# Revit family: KS ALU-PU 80, DS 30, m.Blz, M10-M12, Ø 17,2-168,3
name_source: partatom
category: HLS-Bauteile
units: mm (PartAtom-declared; Revit-internal decimal feet)

## family parameters
Arbeitsebenenbasiert = Ja
Beim Laden mit Abzugskörper schneiden = Nein
Bemaßung runder Anschluss = Durchmesser verwenden
Beschriftungsausrichtung beibehalten = Nein
Gemeinsam genutzt = Ja
Immer vertikal = Nein
Raumberechnungspunkt = Nein
Teiletyp = Normal

## types (19) — shared parameters
Anschluss = M10/M12
Baustoffklasse = B2
DS = 30 mm  [stored 0.0984252 ft]
DVS = 18 mm  [stored 0.0590551 ft]
Dichte Kern = 80 kg/m³
Dichte Mantel = 2700 kg/m³
Dicke Mantel = 0.08 mm
Druckverteilung = Blechzylinder
Dämmkörper = ALU/PU
Dämmstärke = 30 mm  [stored 0.0984252 ft]
Fabrikat = MEFA
Firma = MEFA Befestigungs- und Montagesysteme GmbH
HGA = 22 mm  [stored 0.0721785 ft]
Kurztext1 = Kälteschelle RG80 ALU/PU
L = 100 mm
Material = Stahl
Material Mantel = Alufolie
Materialname = S235
Mengeneinheit = St
Oberflaeche = galvanisch verzinkt
Rohrschellentyp = Maxima PSM
Schalenlänge = 100 mm
Vorgabe-Ansicht = 1219 mm
Wasserdampfdiffusionswiderstand = 18750 µ
Wärmeleitfähigkeit = 0.025 W/mK
max. Temperaturbeständigkeit = 120 °C
mittl. Nenndruckfestigkeit Kern = 0.5 N/mm²
stat. Belastung Kern = 0.1 N/mm²
vpe = 1

## per-type parameters (varying)
- Kälteschelle ALU-PU 80, DS 30, m.Blz, M10/M12, Ø 17,2: A=55 mm  [stored 0.180446 ft]; AB=2 mm  [stored 0.00656168 ft]; Anschlußhöhe=55 mm; Artikelnummer=7590182/B; B=135 mm; Breite=141 mm; D=18 mm  [stored 0.0590551 ft]; D0=78 mm; DF1=25 mm  [stored 0.082021 ft]; DF2=25 mm  [stored 0.082021 ft]; Dmax=19 mm  [stored 0.062336 ft]; Dmin=16 mm  [stored 0.0524934 ft]; EAN=4250928443878; Gewicht=0.54 kg; Gewicht pro Bauteil=0.54 kg; H=106 mm; Kurztext2=17,2 mm Iso 30 x 100 mm M10/M12; MB=30 mm  [stored 0.0984252 ft]; MD=3 mm  [stored 0.00984252 ft]; R=39 mm  [stored 0.127953 ft]; RM=42 mm  [stored 0.137795 ft]; Rohraußendurchmesser Kupfer=18 mm; Rohraußendurchmesser Stahl=17,2 mm; S=110 mm; max. zul. Last=0.30 kN
- Kälteschelle ALU-PU 80, DS 30, m.Blz, M10/M12, Ø 21,3: A=55 mm  [stored 0.180446 ft]; AB=2 mm  [stored 0.00656168 ft]; Anschlußhöhe=56 mm; Artikelnummer=75902142/B; B=150 mm; Breite=151 mm; D=22 mm  [stored 0.0721785 ft]; D0=82 mm; DF1=30 mm  [stored 0.0984252 ft]; DF2=29 mm  [stored 0.0951444 ft]; Dmax=25 mm  [stored 0.082021 ft]; Dmin=20 mm  [stored 0.0656168 ft]; EAN=4250928443892; Gewicht=0.57 kg; Gewicht pro Bauteil=0.57 kg; H=110 mm; Kurztext2=21,3 mm Iso 30 x 100 mm M10/M12; MB=30 mm  [stored 0.0984252 ft]; MD=3 mm  [stored 0.00984252 ft]; R=41 mm  [stored 0.134514 ft]; RM=44 mm  [stored 0.144357 ft]; Rohraußendurchmesser Kupfer=22 mm; Rohraußendurchmesser Stahl=21,3 mm; S=120 mm; max. zul. Last=0.30 kN
- Kälteschelle ALU-PU 80, DS 30, m.Blz, M10/M12, Ø 26,9: A=55 mm  [stored 0.180446 ft]; AB=3 mm  [stored 0.00984252 ft]; Anschlußhöhe=55 mm; Artikelnummer=75902742/B; B=150 mm; Breite=151 mm; D=28 mm  [stored 0.0918635 ft]; D0=88 mm; DF1=27 mm  [stored 0.0885827 ft]; DF2=27 mm  [stored 0.0885827 ft]; Dmax=30 mm  [stored 0.0984252 ft]; Dmin=25 mm  [stored 0.082021 ft]; EAN=4250928443915; Gewicht=0.58 kg; Gewicht pro Bauteil=0.58 kg; H=116 mm; Kurztext2=26,9 mm Iso 30 x 100 mm M10/M12; MB=30 mm  [stored 0.0984252 ft]; MD=3 mm  [stored 0.00984252 ft]; R=44 mm  [stored 0.144357 ft]; RM=47 mm  [stored 0.154199 ft]; Rohraußendurchmesser Kupfer=28 mm; Rohraußendurchmesser Stahl=26,9 mm; S=123 mm; max. zul. Last=0.40 kN
- Kälteschelle ALU-PU 80, DS 30, m.Blz, M10/M12, Ø 33,7: A=55 mm  [stored 0.180446 ft]; AB=3 mm  [stored 0.00984252 ft]; Anschlußhöhe=56 mm; Artikelnummer=75903442/B; B=162 mm; Breite=162 mm; D=35 mm  [stored 0.114829 ft]; D0=95 mm; DF1=30 mm  [stored 0.0984252 ft]; DF2=30 mm  [stored 0.0984252 ft]; Dmax=36 mm  [stored 0.11811 ft]; Dmin=32 mm  [stored 0.104987 ft]; EAN=4250928443939; Gewicht=0.62 kg; Gewicht pro Bauteil=0.62 kg; H=123 mm; Kurztext2=33,7 mm Iso 30 x 100 mm M10/M12; MB=30 mm  [stored 0.0984252 ft]; MD=3 mm  [stored 0.00984252 ft]; R=48 mm; RM=51 mm; Rohraußendurchmesser Kupfer=35 mm; Rohraußendurchmesser Stahl=33,7 mm; S=132 mm; max. zul. Last=0.50 kN
- Kälteschelle ALU-PU 80, DS 30, m.Blz, M10/M12, Ø 42,4: A=55 mm  [stored 0.180446 ft]; AB=2 mm  [stored 0.00656168 ft]; Anschlußhöhe=57 mm; Artikelnummer=75904242/B; B=172 mm; Breite=172 mm; D=42 mm  [stored 0.137795 ft]; D0=102 mm; DF1=31 mm  [stored 0.101706 ft]; DF2=31 mm  [stored 0.101706 ft]; Dmax=44 mm  [stored 0.144357 ft]; Dmin=40 mm  [stored 0.131234 ft]; EAN=4250928443953; Gewicht=0.67 kg; Gewicht pro Bauteil=0.67 kg; H=130 mm; Kurztext2=42,4 mm Iso 30 x 100 mm M10/M12; MB=30 mm  [stored 0.0984252 ft]; MD=3 mm  [stored 0.00984252 ft]; R=51 mm; RM=54 mm  [stored 0.177165 ft]; Rohraußendurchmesser Kupfer=42 mm; Rohraußendurchmesser Stahl=42,4 mm; S=141 mm; max. zul. Last=0.60 kN
- Kälteschelle ALU-PU 80, DS 30, m.Blz, M10/M12, Ø 48,3: A=55 mm  [stored 0.180446 ft]; AB=2 mm  [stored 0.00656168 ft]; Anschlußhöhe=55 mm; Artikelnummer=75904842/B; B=172 mm; Breite=172 mm; D=48 mm; D0=108 mm; DF1=28 mm  [stored 0.0918635 ft]; DF2=28 mm  [stored 0.0918635 ft]; Dmax=50 mm  [stored 0.164042 ft]; Dmin=46 mm  [stored 0.150919 ft]; EAN=4250928443977; Gewicht=0.67 kg; Gewicht pro Bauteil=0.67 kg; H=136 mm; Kurztext2=48,3 mm Iso 30 x 100 mm M10/M12; MB=30 mm  [stored 0.0984252 ft]; MD=3 mm  [stored 0.00984252 ft]; R=54 mm  [stored 0.177165 ft]; RM=57 mm  [stored 0.187008 ft]; Rohraußendurchmesser Stahl=48,3 mm; S=144 mm; max. zul. Last=0.70 kN
- Kälteschelle ALU-PU 80, DS 30, m.Blz, M10/M12, Ø 54: A=55 mm  [stored 0.180446 ft]; AB=4 mm  [stored 0.0131234 ft]; Anschlußhöhe=55 mm; Artikelnummer=75905442/B; B=178 mm; Breite=178 mm; D=54 mm  [stored 0.177165 ft]; D0=114 mm; DF1=28 mm  [stored 0.0918635 ft]; DF2=28 mm  [stored 0.0918635 ft]; Dmax=56 mm  [stored 0.183727 ft]; Dmin=50 mm  [stored 0.164042 ft]; EAN=4250928443991; Gewicht=0.71 kg; Gewicht pro Bauteil=0.71 kg; H=142 mm; Kurztext2=54 mm Iso 30 x 100 mm M10/M12; MB=30 mm  [stored 0.0984252 ft]; MD=3 mm  [stored 0.00984252 ft]; R=57 mm  [stored 0.187008 ft]; RM=60 mm; Rohraußendurchmesser Kupfer=54 mm; S=150 mm; max. zul. Last=0.70 kN
- Kälteschelle ALU-PU 80, DS 30, m.Blz, M10/M12, Ø 57: A=55 mm  [stored 0.180446 ft]; AB=2 mm  [stored 0.00656168 ft]; Anschlußhöhe=54 mm; Artikelnummer=75905742/B; B=178 mm; Breite=178 mm; D=57 mm  [stored 0.187008 ft]; D0=117 mm; DF1=28 mm  [stored 0.0918635 ft]; DF2=27 mm  [stored 0.0885827 ft]; Dmax=57 mm  [stored 0.187008 ft]; Dmin=55 mm  [stored 0.180446 ft]; EAN=4250928444011; Gewicht=0.71 kg; Gewicht pro Bauteil=0.71 kg; H=145 mm; Kurztext2=57 mm Iso 30 x 100 mm M10/M12; MB=30 mm  [stored 0.0984252 ft]; MD=3 mm  [stored 0.00984252 ft]; R=59 mm; RM=62 mm  [stored 0.203412 ft]; Rohraußendurchmesser Stahl=57 mm; S=150 mm; max. zul. Last=0.80 kN
- Kälteschelle ALU-PU 80, DS 30, m.Blz, M10/M12, Ø 60,3: A=55 mm  [stored 0.180446 ft]; AB=2 mm  [stored 0.00656168 ft]; Anschlußhöhe=55 mm; Artikelnummer=75906042/B; B=184 mm; Breite=184 mm; D=60 mm; D0=120 mm; DF1=28 mm  [stored 0.0918635 ft]; DF2=28 mm  [stored 0.0918635 ft]; Dmax=62 mm  [stored 0.203412 ft]; Dmin=58 mm  [stored 0.190289 ft]; EAN=4250928444035; Gewicht=0.73 kg; Gewicht pro Bauteil=0.73 kg; H=148 mm; Kurztext2=60,3 mm Iso 30 x 100 mm M10/M12; MB=30 mm  [stored 0.0984252 ft]; MD=3 mm  [stored 0.00984252 ft]; R=60 mm; RM=63 mm; Rohraußendurchmesser Stahl=60,3 mm; S=156 mm; max. zul. Last=0.90 kN
- Kälteschelle ALU-PU 80, DS 30, m.Blz, M10/M12, Ø 63,5: A=55 mm  [stored 0.180446 ft]; AB=3 mm  [stored 0.00984252 ft]; Anschlußhöhe=56 mm; Artikelnummer=75906442/B; B=189 mm; Breite=189 mm; D=64 mm  [stored 0.209974 ft]; D0=124 mm; DF1=30 mm  [stored 0.0984252 ft]; DF2=29 mm  [stored 0.0951444 ft]; Dmax=64 mm  [stored 0.209974 ft]; Dmin=61 mm  [stored 0.200131 ft]; EAN=4250928444059; Gewicht=0.76 kg; Gewicht pro Bauteil=0.76 kg; H=152 mm; Kurztext2=63,5 mm Iso 30 x 100 mm M10/M12; MB=30 mm  [stored 0.0984252 ft]; MD=3 mm  [stored 0.00984252 ft]; R=62 mm  [stored 0.203412 ft]; RM=65 mm; Rohraußendurchmesser Stahl=63,5 mm; S=159 mm; max. zul. Last=0.90 kN
- Kälteschelle ALU-PU 80, DS 30, m.Blz, M10/M12, Ø 76,1: A=56 mm  [stored 0.183727 ft]; AB=2 mm  [stored 0.00656168 ft]; Anschlußhöhe=57 mm; Artikelnummer=75907644/B; B=217 mm; Breite=216 mm; D=76 mm; D0=136 mm; DF1=35 mm  [stored 0.114829 ft]; DF2=36 mm  [stored 0.11811 ft]; Dmax=78 mm; Dmin=74 mm; EAN=4250928444097; Gewicht=1.03 kg; Gewicht pro Bauteil=1.03 kg; H=166 mm; Kurztext2=76,1 mm Iso 30 x 100 mm M10/M12; MB=35 mm  [stored 0.114829 ft]; MD=4 mm  [stored 0.0131234 ft]; R=68 mm; RM=72 mm; Rohraußendurchmesser Stahl=76,1 mm; S=182 mm; max. zul. Last=1.10 kN
- Kälteschelle ALU-PU 80, DS 30, m.Blz, M10/M12, Ø 88,9: A=56 mm  [stored 0.183727 ft]; AB=1 mm  [stored 0.00328084 ft]; Anschlußhöhe=56 mm; Artikelnummer=75908944/B; B=227 mm; Breite=226 mm; D=89 mm; D0=149 mm; DF1=34 mm; DF2=35 mm  [stored 0.114829 ft]; Dmax=90 mm; Dmin=88 mm; EAN=4250928444110; Gewicht=1.12 kg; Gewicht pro Bauteil=1.12 kg; H=179 mm; Kurztext2=88,9 mm Iso 30 x 100 mm M10/M12; MB=35 mm  [stored 0.114829 ft]; MD=4 mm  [stored 0.0131234 ft]; R=74 mm; RM=78 mm; Rohraußendurchmesser Stahl=88,9 mm; S=193 mm; max. zul. Last=1.30 kN
- Kälteschelle ALU-PU 80, DS 30, m.Blz, M10/M12, Ø108: A=56 mm  [stored 0.183727 ft]; AB=2 mm  [stored 0.00656168 ft]; Anschlußhöhe=57 mm; Artikelnummer=75910844/B; B=248 mm; Breite=247 mm; D=108 mm; D0=168 mm; DF1=35 mm  [stored 0.114829 ft]; DF2=35 mm  [stored 0.114829 ft]; Dmax=110 mm; Dmin=106 mm; EAN=4250928444134; Gewicht=1.22 kg; Gewicht pro Bauteil=1.22 kg; H=198 mm; Kurztext2=108 mm Iso 30 x 100 mm M10/M12; MB=35 mm  [stored 0.114829 ft]; MD=4 mm  [stored 0.0131234 ft]; R=84 mm; RM=88 mm; Rohraußendurchmesser Stahl=108 mm; S=213 mm; max. zul. Last=1.60 kN
- Kälteschelle ALU-PU 80, DS 30, m.Blz, M10/M12, Ø114,3: A=56 mm  [stored 0.183727 ft]; AB=2 mm  [stored 0.00656168 ft]; Anschlußhöhe=57 mm; Artikelnummer=75911444/B; B=253 mm; Breite=252 mm; D=114 mm; D0=174 mm; DF1=34 mm; DF2=35 mm  [stored 0.114829 ft]; Dmax=116 mm; Dmin=112 mm; EAN=4250928444158; Gewicht=1.25 kg; Gewicht pro Bauteil=1.25 kg; H=204 mm; Kurztext2=114,3 mm Iso 30 x 100 mm M10/M12; MB=35 mm  [stored 0.114829 ft]; MD=4 mm  [stored 0.0131234 ft]; R=87 mm; RM=91 mm; Rohraußendurchmesser Stahl=114.3 mm; S=219 mm; max. zul. Last=1.70 kN
- Kälteschelle ALU-PU 80, DS 30, m.Blz, M10/M12, Ø133: A=56 mm  [stored 0.183727 ft]; AB=1 mm  [stored 0.00328084 ft]; Anschlußhöhe=57 mm; Artikelnummer=75913344/B; B=273 mm; Breite=272 mm; D=133 mm; D0=193 mm; DF1=34 mm; DF2=35 mm  [stored 0.114829 ft]; Dmax=136 mm; Dmin=132 mm; EAN=4250928444196; Gewicht=1.37 kg; Gewicht pro Bauteil=1.37 kg; H=223 mm; Kurztext2=133 mm Iso 30 x 100 mm M10/M12; MB=35 mm  [stored 0.114829 ft]; MD=4 mm  [stored 0.0131234 ft]; R=97 mm; RM=101 mm; Rohraußendurchmesser Stahl=133 mm; S=239 mm; max. zul. Last=1.90 kN
- Kälteschelle ALU-PU 80, DS 30, m.Blz, M10/M12, Ø139,7: A=56 mm  [stored 0.183727 ft]; AB=2 mm  [stored 0.00656168 ft]; Anschlußhöhe=57 mm; Artikelnummer=75914044/B; B=279 mm; Breite=278 mm; D=140 mm; D0=200 mm; DF1=35 mm  [stored 0.114829 ft]; DF2=36 mm  [stored 0.11811 ft]; Dmax=140 mm; Dmin=138 mm; EAN=4250928444233; Gewicht=1.41 kg; Gewicht pro Bauteil=1.41 kg; H=230 mm; Kurztext2=139,7 mm Iso 30 x 100 mm M10/M12; MB=35 mm  [stored 0.114829 ft]; MD=4 mm  [stored 0.0131234 ft]; R=100 mm; RM=104 mm; Rohraußendurchmesser Stahl=139,7 mm; S=244 mm; max. zul. Last=2.00 kN
- Kälteschelle ALU-PU 80, DS 30, m.Blz, M10/M12, Ø159: A=56 mm  [stored 0.183727 ft]; AB=1 mm  [stored 0.00328084 ft]; Anschlußhöhe=56 mm; Artikelnummer=75915944/B; B=298 mm; Breite=297 mm; D=159 mm; D0=219 mm; DF1=35 mm  [stored 0.114829 ft]; DF2=35 mm  [stored 0.114829 ft]; Dmax=160 mm; Dmin=158 mm; EAN=4250928444271; Gewicht=1.51 kg; Gewicht pro Bauteil=1.51 kg; H=249 mm; Kurztext2=159 mm Iso 30 x 100 mm M10/M12; MB=35 mm  [stored 0.114829 ft]; MD=4 mm  [stored 0.0131234 ft]; R=110 mm; RM=114 mm; Rohraußendurchmesser Stahl=159 mm; S=263 mm; max. zul. Last=2.30 kN
- Kälteschelle ALU-PU 80, DS 30, m.Blz, M10/M12, Ø168,3: A=56 mm  [stored 0.183727 ft]; AB=2 mm  [stored 0.00656168 ft]; Anschlußhöhe=57 mm; Artikelnummer=75916844/B; B=308 mm; Breite=308 mm; D=168 mm; D0=228 mm; DF1=35 mm  [stored 0.114829 ft]; DF2=35 mm  [stored 0.114829 ft]; Dmax=170 mm; Dmin=166 mm; EAN=4250928444295; Gewicht=1.58 kg; Gewicht pro Bauteil=1.58 kg; H=258 mm; Kurztext2=168,3 mm Iso 30 x 100 mm M10/M12; MB=35 mm  [stored 0.114829 ft]; MD=4 mm  [stored 0.0131234 ft]; R=114 mm; RM=118 mm; Rohraußendurchmesser Stahl=168,3 mm; S=273 mm; max. zul. Last=2.50 kN
- Kälteschelle ALU-PU 80, DS 30, m.Blz, M10/M12, Ø 70: A=56 mm  [stored 0.183727 ft]; AB=2 mm  [stored 0.00656168 ft]; Anschlußhöhe=57 mm; Artikelnummer=75907042/B; B=210 mm; Breite=209 mm; D=70 mm; D0=130 mm; DF1=35 mm  [stored 0.114829 ft]; DF2=35 mm  [stored 0.114829 ft]; Dmax=72 mm; Dmin=68 mm; EAN=4250928444073; Gewicht=1.00 kg; Gewicht pro Bauteil=1.00 kg; H=160 mm; Kurztext2=70 mm Iso 30 x 100 mm M10/M12; MB=35 mm  [stored 0.114829 ft]; MD=4 mm  [stored 0.0131234 ft]; R=65 mm; RM=69 mm; Rohraußendurchmesser Stahl=70 mm; S=175 mm; max. zul. Last=1.00 kN

note: [stored X ft] marks values corroborated as IEEE doubles in the binary element streams (Revit-internal decimal feet)

## geometry (parser evidence)
native form markers: Sweep x4
no freeform markers — native parametric forms only
